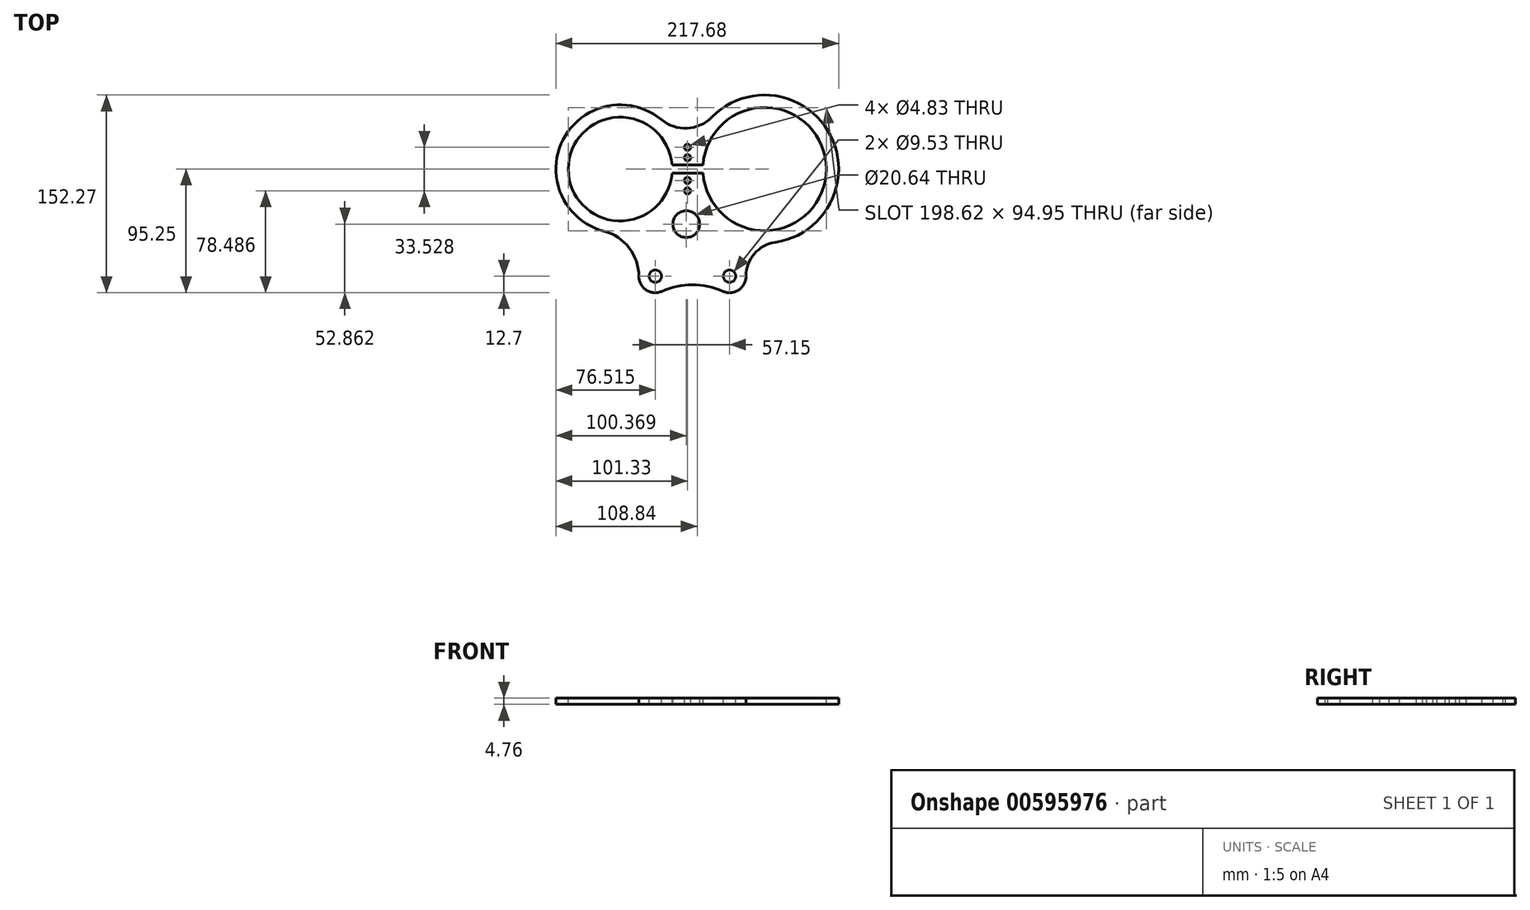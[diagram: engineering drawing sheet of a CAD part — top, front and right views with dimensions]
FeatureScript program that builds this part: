
annotation { "Feature Type Name" : "Feature", "Feature Type Description" : "" }
export const myFeature = defineFeature(function(context is Context, id is Id, definition is map)
    precondition{}
    {
        {
            var Q0;
            Q0=qCreatedBy(makeId("Top.planeOp"),FACE);
            var sketch = newSketch(context, id + "F0", { "sketchPlane" : qUnion([Q0])});
            skCircle(sketch, "E0", {"center": v(-55.56, 38.1) * mm, "radius": 40 * mm});
            skCircle(sketch, "E1", {"center": v(55.56, 38.1) * mm, "radius": 47.5 * mm});
            skCircle(sketch, "E2", {"center": v(-4.72, -4.29) * mm, "radius": 10.32 * mm});
            skCircle(sketch, "E3", {"center": v(-28.58, -44.45) * mm, "radius": 4.76 * mm});
            skArc(sketch, "E4", {"start": v(14.95, 78.14) * mm, "mid": v(106.43, 63.88) * mm, "end": v(63.85, -18.32) * mm});
            skArc(sketch, "E5", {"start": v(-23.92, 76.2) * mm, "mid": v(-99.63, 60.7) * mm, "end": v(-68.04, -9.83) * mm});
            skArc(sketch, "E6", {"start": v(-23.47, -56.08) * mm, "mid": v(-35.52, -55.08) * mm, "end": v(-41.28, -44.45) * mm});
            skArc(sketch, "E7.MirrorCS", {"start": v(23.47, -56.08) * mm, "mid": v(35.52, -55.08) * mm, "end": v(41.28, -44.45) * mm});
            skCircle(sketch, "E8.MirrorC", {"center": v(28.58, -44.45) * mm, "radius": 4.76 * mm});
            skArc(sketch, "E9", {"start": v(-23.47, -56.08) * mm, "mid": v(0, -51.15) * mm, "end": v(23.47, -56.08) * mm});
            skArc(sketch, "E10", {"start": v(63.85, -18.32) * mm, "mid": v(47.7, -27.18) * mm, "end": v(41.28, -44.45) * mm});
            skArc(sketch, "E11", {"start": v(-68.04, -9.83) * mm, "mid": v(-48.75, -22.57) * mm, "end": v(-41.27, -44.45) * mm});
            skArc(sketch, "E12", {"start": v(-23.92, 76.2) * mm, "mid": v(-4.1, 69.6) * mm, "end": v(14.95, 78.14) * mm});
            skLineSegment(sketch, "E13", {"start": v(-15.69, 41.28) * mm, "end": v(8.17, 41.28) * mm});
            skLineSegment(sketch, "E14", {"start": v(-15.69, 34.93) * mm, "end": v(8.17, 34.93) * mm});
            skCircle(sketch, "E15", {"center": v(-3.76, 46.86) * mm, "radius": 2.41 * mm});
            skCircle(sketch, "E16", {"center": v(-3.76, 54.86) * mm, "radius": 2.41 * mm});
            skCircle(sketch, "E17", {"center": v(-3.76, 29.34) * mm, "radius": 2.41 * mm});
            skPoint(sketch, "E17.centerSnap0", {"position": v(-3.76, 34.93) * mm});
            skCircle(sketch, "E18", {"center": v(-3.76, 21.34) * mm, "radius": 2.41 * mm});
            skLineSegment(sketch, "E19", {"start": v(-45.83, -26.99) * mm, "end": v(47.87, -26.99) * mm});
            skSolve(sketch);
        }
        {
            var Q0;
            Q0=makeQuery(id+"F0.imprint","IMPRINT",FACE,{"disambiguationData":[TD([[makeQuery(id+"F0.imprint","IMPRINT",EDGE,{"derivedFrom":sQuery(id+"F0.wireOp",EDGE,"E3")}),-1.0]])]});
            var Q1;
            Q1=makeQuery(id+"F0.imprint","IMPRINT",FACE,{"disambiguationData":[TD([[makeQuery(id+"F0.imprint","IMPRINT",EDGE,{"derivedFrom":sQuery(id+"F0.wireOp",EDGE,"E2")}),-1.0]])]});
            extrude(context, id + "F1", {"entities" : qUnion([Q0, Q1]), "oppositeDirection" : true, "depth" : 4.76 * mm, "offsetDistance" : 25.4 * mm});
        }
    });
